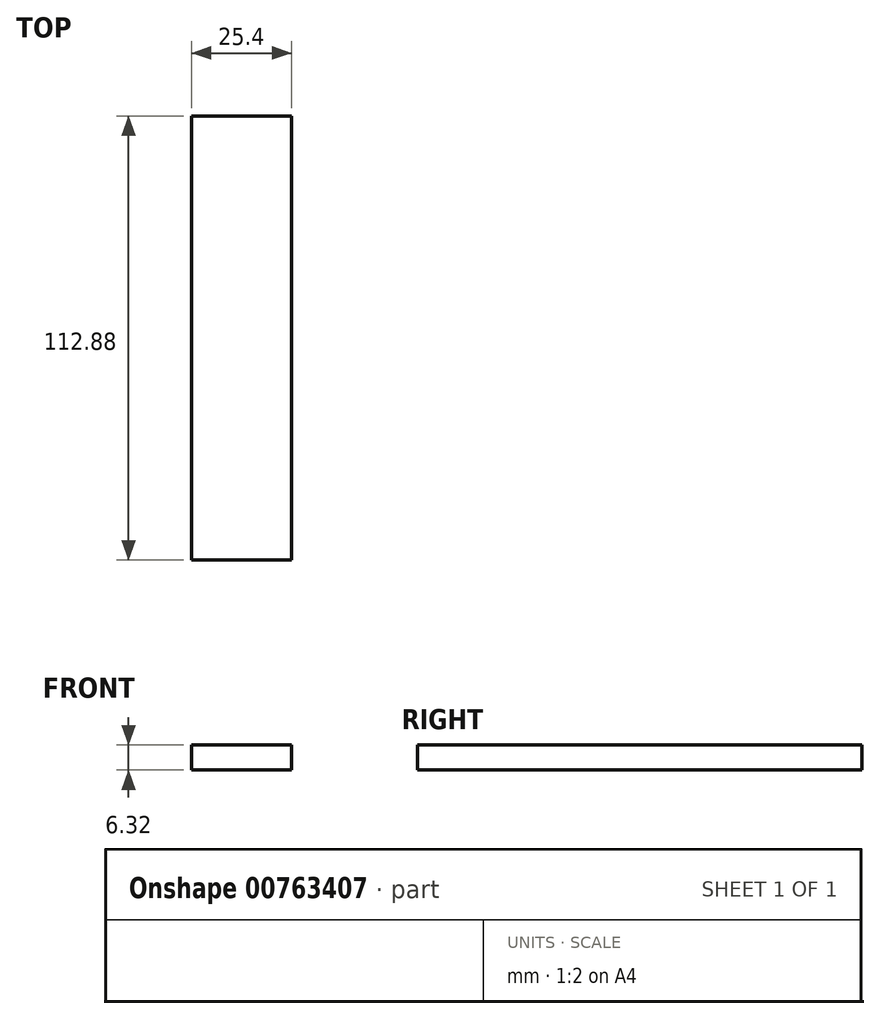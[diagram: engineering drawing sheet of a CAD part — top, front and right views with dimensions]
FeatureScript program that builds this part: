
annotation { "Feature Type Name" : "Feature", "Feature Type Description" : "" }
export const myFeature = defineFeature(function(context is Context, id is Id, definition is map)
    precondition{}
    {
        {
            var Q0;
            Q0=qCreatedBy(makeId("Right.planeOp"),FACE);
            var sketch = newSketch(context, id + "F0", { "sketchPlane" : qUnion([Q0])});
            skLineSegment(sketch, "E0.bottom", {"start": v(56.44, 0) * mm, "end": v(-56.44, 0) * mm});
            skLineSegment(sketch, "E0.top", {"start": v(56.44, -6.32) * mm, "end": v(-56.44, -6.32) * mm});
            skLineSegment(sketch, "E0.left", {"start": v(56.44, 0) * mm, "end": v(56.44, -6.32) * mm});
            skLineSegment(sketch, "E0.right", {"start": v(-56.44, 0) * mm, "end": v(-56.44, -6.32) * mm});
            skPoint(sketch, "E0.middle", {"position": v(0, -3.16) * mm});
            skSolve(sketch);
        }
        {
            var Q0;
            Q0 = qSketchRegion(id + "F0", true);
            extrude(context, id + "F1", {"entities" : qUnion([Q0]), "depth" : 25.4 * mm, "offsetDistance" : 25.4 * mm});
        }
    });
